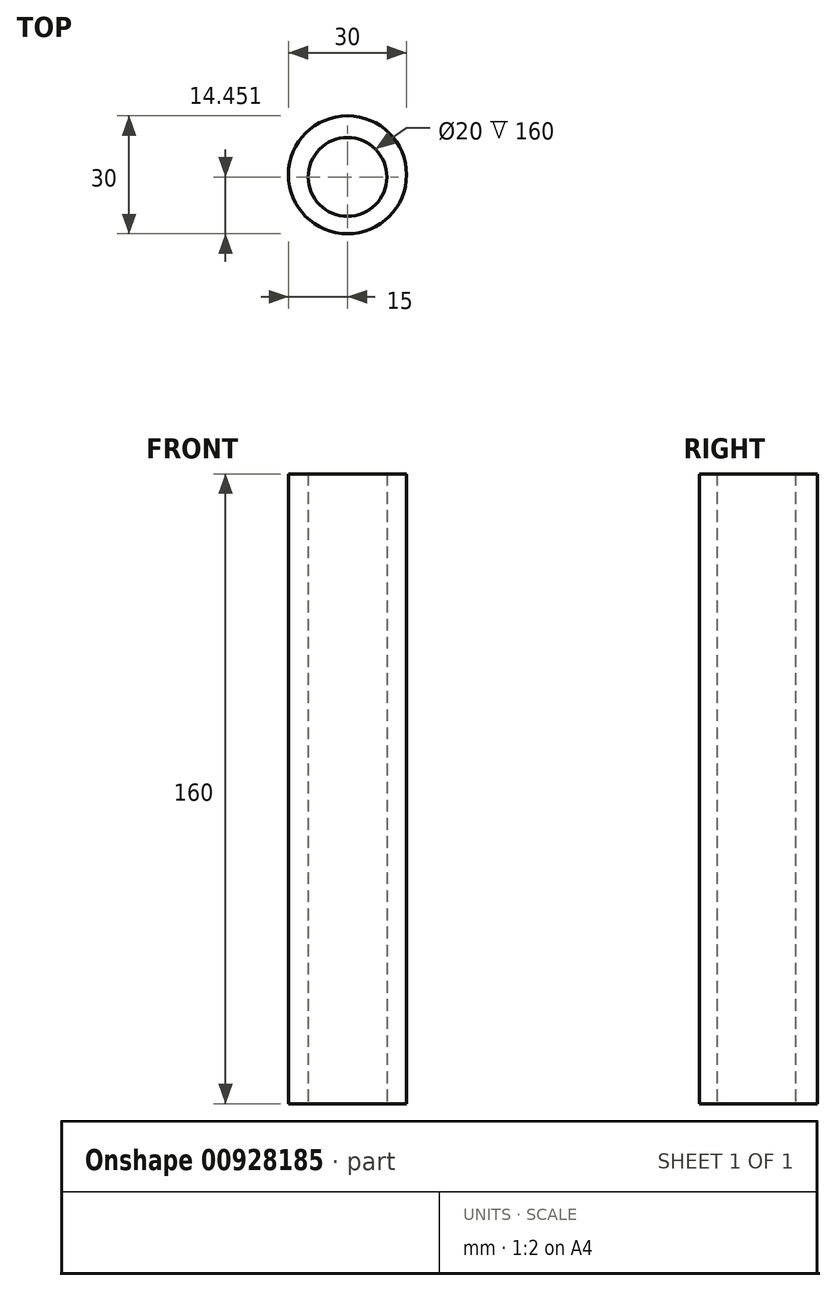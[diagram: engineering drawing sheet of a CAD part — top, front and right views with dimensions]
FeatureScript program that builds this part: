
annotation { "Feature Type Name" : "Feature", "Feature Type Description" : "" }
export const myFeature = defineFeature(function(context is Context, id is Id, definition is map)
    precondition{}
    {
        {
            var Q0;
            Q0=qCreatedBy(makeId("Top.planeOp"),FACE);
            var sketch = newSketch(context, id + "F0", { "sketchPlane" : qUnion([Q0])});
            skCircle(sketch, "E0", {"center": v(0, 0) * mm, "radius": 15 * mm});
            skCircle(sketch, "E1", {"center": v(0, -0.55) * mm, "radius": 10 * mm});
            skSolve(sketch);
        }
        {
            var Q0;
            Q0 = qSketchRegion(id + "F0", true);
            extrude(context, id + "F1", {"entities" : qUnion([Q0]), "depth" : 160 * mm, "offsetDistance" : 25 * mm});
        }
    });
